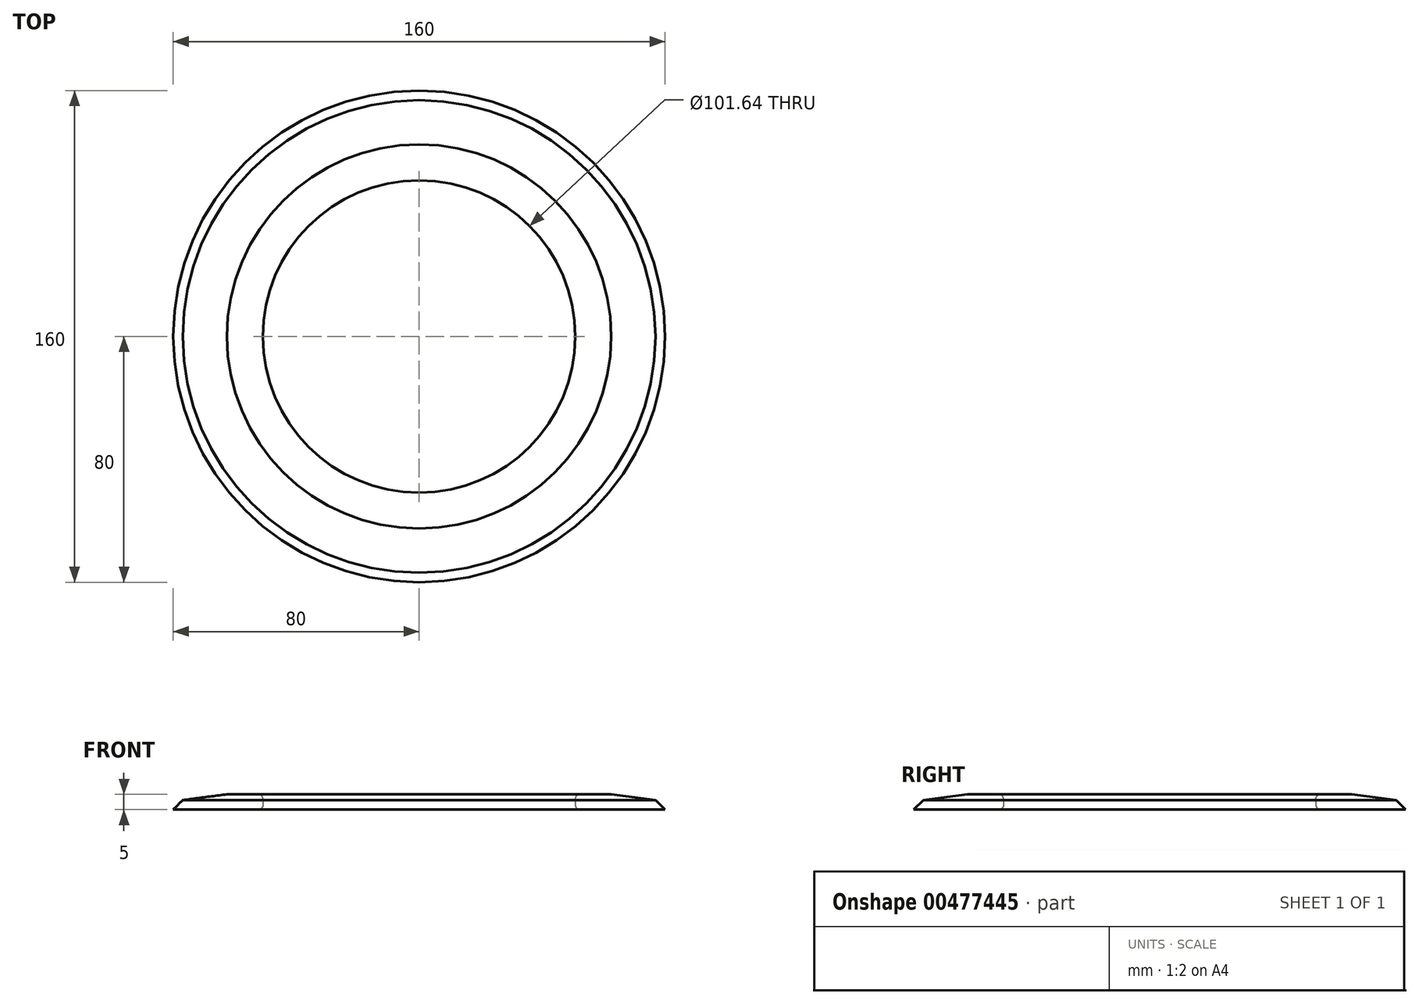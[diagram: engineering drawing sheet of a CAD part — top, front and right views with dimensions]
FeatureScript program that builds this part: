
annotation { "Feature Type Name" : "Feature", "Feature Type Description" : "" }
export const myFeature = defineFeature(function(context is Context, id is Id, definition is map)
    precondition{}
    {
        {
            var Q0;
            Q0=qCreatedBy(makeId("Top.planeOp"),FACE);
            var sketch = newSketch(context, id + "F0", { "sketchPlane" : qUnion([Q0])});
            skCircle(sketch, "E0", {"center": v(0, 0) * mm, "radius": 80 * mm});
            skCircle(sketch, "E1", {"center": v(0, 0) * mm, "radius": 50.82 * mm});
            skSolve(sketch);
        }
        {
            var Q0;
            Q0 = qSketchRegion(id + "F0", true);
            extrude(context, id + "F1", {"entities" : qUnion([Q0]), "depth" : 5 * mm, "offsetDistance" : 25 * mm});
        }
        {
            var Q0;
            Q0=makeQuery(id+"F1.opExtrude","CAP_EDGE",EDGE,{"disambiguationData":[OSD([sQuery(id+"F0.wireOp",EDGE,"E0")])],"isStart":false});
            chamfer(context, id + "F2", {"entities" : qUnion([Q0]), "width" : 5 * mm, "tangentPropagation" : true});
        }
        {
            var Q0;
            {var subQ0=sQuery(id+"F0.wireOp",EDGE,"E0");Q0=makeQuery(id+"F2.opChamfer","BLEND_EDGE",EDGE,{"blendedFrom":[makeQuery(id+"F1.opExtrude","CAP_EDGE",EDGE,{"disambiguationData":[OSD([subQ0])],"isStart":false}),makeQuery(id+"F1.opExtrude","CAP_FACE",FACE,{"disambiguationData":[OSD([subQ0,sQuery(id+"F0.wireOp",EDGE,"E1")])],"isStart":false})],"blendedInto":[makeQuery(id+"F1.opExtrude","CAP_FACE",FACE,{"disambiguationData":[OSD([subQ0,sQuery(id+"F0.wireOp",EDGE,"E1")])],"isStart":false})]});}
            chamfer(context, id + "F3", {"entities" : qUnion([Q0]), "width" : 6 * mm, "tangentPropagation" : true});
        }
        {
            var Q0;
            Q0=makeQuery(id+"F1.opExtrude","CAP_EDGE",EDGE,{"disambiguationData":[OSD([sQuery(id+"F0.wireOp",EDGE,"E1")])],"isStart":false});
            fillet(context, id + "F4", {"entities" : qUnion([Q0]), "radius" : 1.5 * mm, "tangentPropagation" : true, "allowEdgeOverflow" : false});
        }
        {
            var Q0;
            Q0=makeQuery(id+"F1.opExtrude","CAP_EDGE",EDGE,{"disambiguationData":[OSD([sQuery(id+"F0.wireOp",EDGE,"E1")])],"isStart":true});
            fillet(context, id + "F5", {"entities" : qUnion([Q0]), "radius" : 1.5 * mm, "tangentPropagation" : true, "allowEdgeOverflow" : false});
        }
        {
            var Q0;
            {var subQ0=sQuery(id+"F0.wireOp",EDGE,"E0");var subQ1=makeQuery(id+"F1.opExtrude","CAP_FACE",FACE,{"disambiguationData":[OSD([subQ0,sQuery(id+"F0.wireOp",EDGE,"E1")])],"isStart":false});Q0=makeQuery(id+"F3.opChamfer","BLEND_EDGE",EDGE,{"blendedFrom":[makeQuery(id+"F2.opChamfer","BLEND_EDGE",EDGE,{"blendedFrom":[makeQuery(id+"F1.opExtrude","CAP_EDGE",EDGE,{"disambiguationData":[OSD([subQ0])],"isStart":false}),subQ1],"blendedInto":[subQ1]}),subQ1],"blendedInto":[subQ1]});}
            chamfer(context, id + "F6", {"entities" : qUnion([Q0]), "chamferType" : ChamferType.TWO_OFFSETS, "width1" : 10 * mm, "oppositeDirection" : false, "width2" : 5 * mm, "tangentPropagation" : true});
        }
    });
